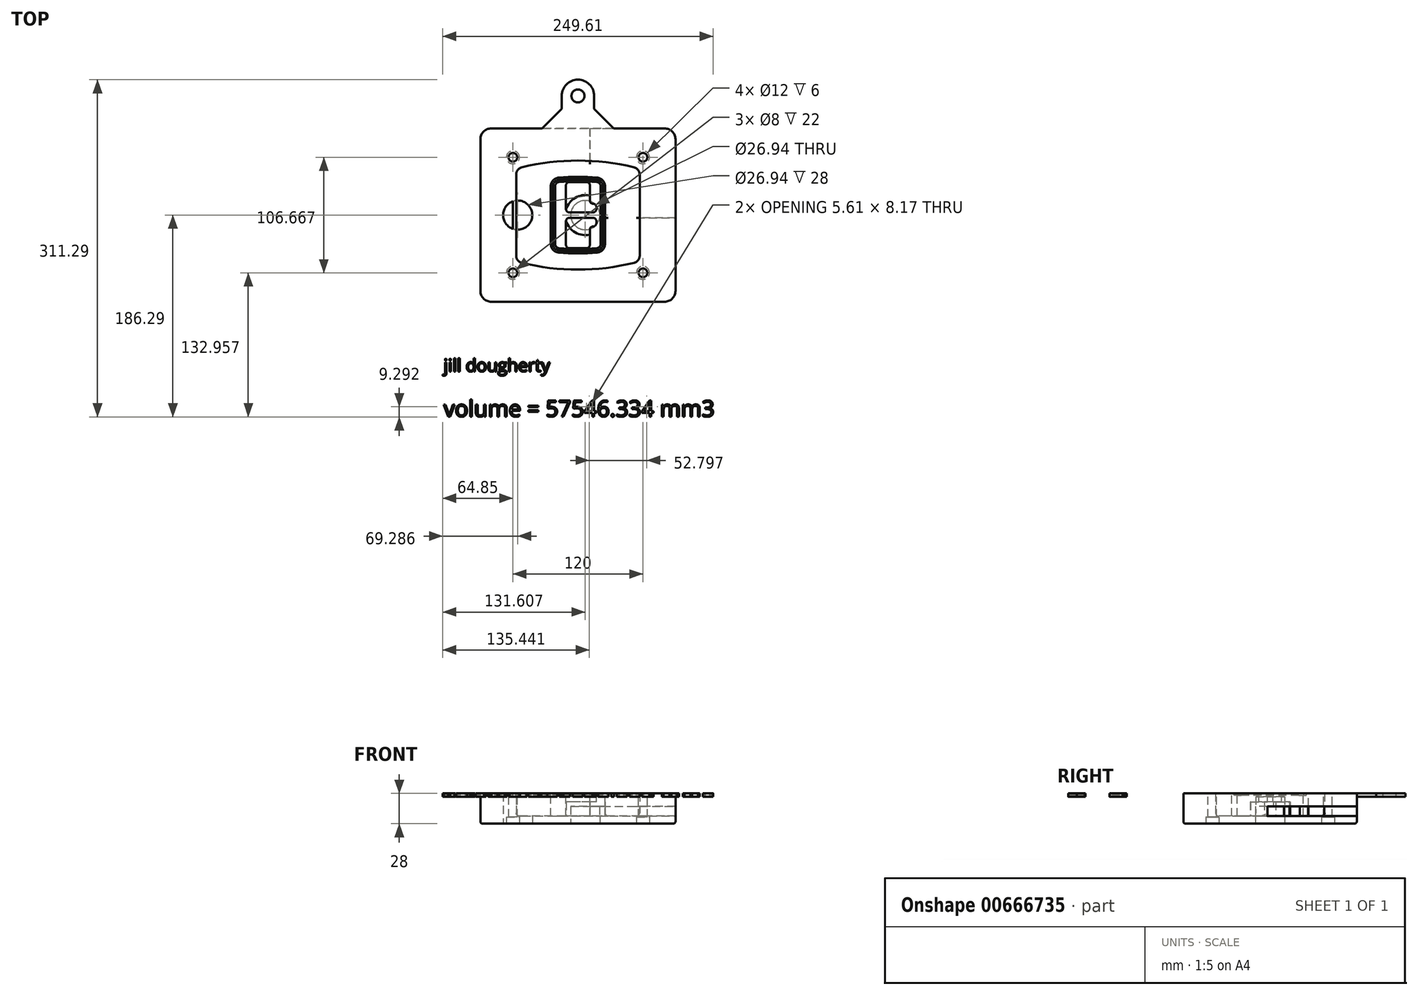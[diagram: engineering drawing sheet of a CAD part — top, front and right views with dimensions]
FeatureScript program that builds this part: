
annotation { "Feature Type Name" : "Feature", "Feature Type Description" : "" }
export const myFeature = defineFeature(function(context is Context, id is Id, definition is map)
    precondition{}
    {
        {
            var Q0;
            Q0=qCreatedBy(makeId("Top.planeOp"),FACE);
            var sketch = newSketch(context, id + "F0", { "sketchPlane" : qUnion([Q0])});
            skPoint(sketch, "E0.rect.middle", {"position": v(0, 0) * mm});
            skLineSegment(sketch, "E1.bottom", {"start": v(-80, -80) * mm, "end": v(80, -80) * mm});
            skLineSegment(sketch, "E1.top", {"start": v(-80, 80) * mm, "end": v(80, 80) * mm});
            skLineSegment(sketch, "E1.left", {"start": v(-90, -70) * mm, "end": v(-90, 70) * mm});
            skLineSegment(sketch, "E1.right", {"start": v(90, -70) * mm, "end": v(90, 70) * mm});
            skLineSegment(sketch, "E2", {"start": v(-90, 80) * mm, "end": v(90, -80) * mm, "construction": true});
            skLineSegment(sketch, "E3", {"start": v(90, 80) * mm, "end": v(-90, -80) * mm, "construction": true});
            skCircle(sketch, "E4", {"center": v(-60, 53.33) * mm, "radius": 4 * mm});
            skCircle(sketch, "E5", {"center": v(60, 53.33) * mm, "radius": 4 * mm});
            skCircle(sketch, "E6", {"center": v(60, -53.33) * mm, "radius": 4 * mm});
            skCircle(sketch, "E7", {"center": v(-60, -53.33) * mm, "radius": 4 * mm});
            skLineSegment(sketch, "E8", {"start": v(-60, 53.33) * mm, "end": v(60, 53.33) * mm, "construction": true});
            skLineSegment(sketch, "E9", {"start": v(60, 53.33) * mm, "end": v(60, -53.33) * mm, "construction": true});
            skLineSegment(sketch, "E10", {"start": v(60, -53.33) * mm, "end": v(-60, -53.33) * mm, "construction": true});
            skLineSegment(sketch, "E11", {"start": v(-60, -53.33) * mm, "end": v(-60, 53.33) * mm, "construction": true});
            skLineSegment(sketch, "E12", {"start": v(-60, 37.3) * mm, "end": v(-60, -37.3) * mm});
            skLineSegment(sketch, "E13", {"start": v(60, 37.3) * mm, "end": v(60, -37.3) * mm});
            skArc(sketch, "E14", {"start": v(52.38, 47.01) * mm, "mid": v(0, 53.33) * mm, "end": v(-52.38, 47.01) * mm});
            skArc(sketch, "E15", {"start": v(-52.38, -47.01) * mm, "mid": v(0, -53.33) * mm, "end": v(52.38, -47.01) * mm});
            skLineSegment(sketch, "E16", {"start": v(-60, 0) * mm, "end": v(60, 0) * mm, "construction": true});
            skPoint(sketch, "E17.visualSharp", {"position": v(-60, -45) * mm});
            skArc(sketch, "E17.filletArc", {"start": v(-60, -37.3) * mm, "mid": v(-57.87, -43.47) * mm, "end": v(-52.38, -47.01) * mm});
            skPoint(sketch, "E18.visualSharp", {"position": v(-60, 45) * mm});
            skArc(sketch, "E18.filletArc", {"start": v(-52.38, 47.01) * mm, "mid": v(-57.87, 43.47) * mm, "end": v(-60, 37.3) * mm});
            skPoint(sketch, "E19.visualSharp", {"position": v(60, 45) * mm});
            skArc(sketch, "E19.filletArc", {"start": v(60, 37.3) * mm, "mid": v(57.87, 43.47) * mm, "end": v(52.38, 47.01) * mm});
            skPoint(sketch, "E20.visualSharp", {"position": v(60, -45) * mm});
            skArc(sketch, "E20.filletArc", {"start": v(52.38, -47.01) * mm, "mid": v(57.87, -43.47) * mm, "end": v(60, -37.3) * mm});
            skPoint(sketch, "E21.visualSharp", {"position": v(-90, 80) * mm});
            skArc(sketch, "E21.filletArc", {"start": v(-80, 80) * mm, "mid": v(-87.07, 77.07) * mm, "end": v(-90, 70) * mm});
            skPoint(sketch, "E22.visualSharp", {"position": v(90, 80) * mm});
            skArc(sketch, "E22.filletArc", {"start": v(90, 70) * mm, "mid": v(87.07, 77.07) * mm, "end": v(80, 80) * mm});
            skPoint(sketch, "E23.visualSharp", {"position": v(90, -80) * mm});
            skArc(sketch, "E23.filletArc", {"start": v(80, -80) * mm, "mid": v(87.07, -77.07) * mm, "end": v(90, -70) * mm});
            skPoint(sketch, "E24.visualSharp", {"position": v(-90, -80) * mm});
            skArc(sketch, "E24.filletArc", {"start": v(-90, -70) * mm, "mid": v(-87.07, -77.07) * mm, "end": v(-80, -80) * mm});
            skArc(sketch, "E25.0", {"start": v(57, 37.3) * mm, "mid": v(55.5, 41.62) * mm, "end": v(51.67, 44.1) * mm});
            skLineSegment(sketch, "E25.1", {"start": v(57, 37.3) * mm, "end": v(57, -37.3) * mm});
            skArc(sketch, "E25.2", {"start": v(51.67, -44.1) * mm, "mid": v(55.5, -41.62) * mm, "end": v(57, -37.3) * mm});
            skArc(sketch, "E25.3", {"start": v(-51.67, -44.1) * mm, "mid": v(0, -50.33) * mm, "end": v(51.67, -44.1) * mm});
            skArc(sketch, "E25.4", {"start": v(-57, -37.3) * mm, "mid": v(-55.5, -41.62) * mm, "end": v(-51.67, -44.1) * mm});
            skArc(sketch, "E25.5", {"start": v(51.67, 44.1) * mm, "mid": v(0, 50.33) * mm, "end": v(-51.67, 44.1) * mm});
            skLineSegment(sketch, "E25.6", {"start": v(-57, 37.3) * mm, "end": v(-57, -37.3) * mm});
            skArc(sketch, "E25.7", {"start": v(-51.67, 44.1) * mm, "mid": v(-55.5, 41.62) * mm, "end": v(-57, 37.3) * mm});
            skArc(sketch, "E26.0", {"start": v(-53.33, 50.9) * mm, "mid": v(-61.01, 45.94) * mm, "end": v(-64, 37.3) * mm});
            skArc(sketch, "E26.1", {"start": v(53.33, 50.9) * mm, "mid": v(0, 57.33) * mm, "end": v(-53.33, 50.9) * mm});
            skArc(sketch, "E26.2", {"start": v(64, 37.3) * mm, "mid": v(61.01, 45.94) * mm, "end": v(53.33, 50.9) * mm});
            skLineSegment(sketch, "E26.3", {"start": v(64, 37.3) * mm, "end": v(64, -37.3) * mm});
            skArc(sketch, "E26.4", {"start": v(53.33, -50.9) * mm, "mid": v(61.01, -45.94) * mm, "end": v(64, -37.3) * mm});
            skLineSegment(sketch, "E26.5", {"start": v(-64, 37.3) * mm, "end": v(-64, -37.3) * mm});
            skArc(sketch, "E26.6", {"start": v(-53.33, -50.9) * mm, "mid": v(0, -57.33) * mm, "end": v(53.33, -50.9) * mm});
            skArc(sketch, "E26.7", {"start": v(-64, -37.3) * mm, "mid": v(-61.01, -45.94) * mm, "end": v(-53.33, -50.9) * mm});
            skSolve(sketch);
        }
        {
            var Q0;
            Q0=makeQuery(id+"F0.imprint","IMPRINT",FACE,{"disambiguationData":[TD([[makeQuery(id+"F0.imprint","IMPRINT",EDGE,{"derivedFrom":sQuery(id+"F0.wireOp",EDGE,"E1.bottom")}),1.0]])]});
            var Q1;
            Q1=makeQuery(id+"F0.imprint","IMPRINT",FACE,{"disambiguationData":[TD([[makeQuery(id+"F0.imprint","IMPRINT",EDGE,{"derivedFrom":sQuery(id+"F0.wireOp",EDGE,"E12")}),1.0]])]});
            var Q2;
            Q2=makeQuery(id+"F0.imprint","IMPRINT",FACE,{"disambiguationData":[TD([[makeQuery(id+"F0.imprint","IMPRINT",EDGE,{"derivedFrom":sQuery(id+"F0.wireOp",EDGE,"E25.0")}),1.0]])]});
            var Q3;
            Q3=makeQuery(id+"F0.imprint","IMPRINT",FACE,{"disambiguationData":[TD([[makeQuery(id+"F0.imprint","IMPRINT",EDGE,{"derivedFrom":sQuery(id+"F0.wireOp",EDGE,"E12")}),-1.0]])]});
            extrude(context, id + "F1", {"entities" : qUnion([Q0, Q1, Q2, Q3]), "oppositeDirection" : true, "depth" : 25 * mm});
        }
        {
            var Q0;
            Q0=makeQuery(id+"F0.imprint","IMPRINT",FACE,{"disambiguationData":[TD([[makeQuery(id+"F0.imprint","IMPRINT",EDGE,{"derivedFrom":sQuery(id+"F0.wireOp",EDGE,"E12")}),1.0]])]});
            extrude(context, id + "F2", {"entities" : qUnion([Q0]), "operationType" : NewBodyOperationType.ADD, "depth" : 3 * mm});
        }
        {
            var Q0;
            Q0=makeQuery(id+"F0.imprint","IMPRINT",FACE,{"disambiguationData":[TD([[makeQuery(id+"F0.imprint","IMPRINT",EDGE,{"derivedFrom":sQuery(id+"F0.wireOp",EDGE,"E25.0")}),1.0]])]});
            extrude(context, id + "F3", {"entities" : qUnion([Q0]), "operationType" : NewBodyOperationType.REMOVE, "oppositeDirection" : true, "depth" : 18 * mm});
        }
        {
            var Q0;
            Q0=makeQuery(id+"F2.opExtrude","CAP_FACE",FACE,{"disambiguationData":[OSD([sQuery(id+"F0.wireOp",EDGE,"E12"),sQuery(id+"F0.wireOp",EDGE,"E13"),sQuery(id+"F0.wireOp",EDGE,"E14"),sQuery(id+"F0.wireOp",EDGE,"E15"),sQuery(id+"F0.wireOp",EDGE,"E17.filletArc"),sQuery(id+"F0.wireOp",EDGE,"E18.filletArc"),sQuery(id+"F0.wireOp",EDGE,"E19.filletArc"),sQuery(id+"F0.wireOp",EDGE,"E20.filletArc"),sQuery(id+"F0.wireOp",EDGE,"E25.0"),sQuery(id+"F0.wireOp",EDGE,"E25.1"),sQuery(id+"F0.wireOp",EDGE,"E25.2"),sQuery(id+"F0.wireOp",EDGE,"E25.3"),sQuery(id+"F0.wireOp",EDGE,"E25.4"),sQuery(id+"F0.wireOp",EDGE,"E25.5"),sQuery(id+"F0.wireOp",EDGE,"E25.6"),sQuery(id+"F0.wireOp",EDGE,"E25.7")])],"isStart":false});
            var sketch = newSketch(context, id + "F4", { "sketchPlane" : qUnion([Q0])});
            skArc(sketch, "E27.0", {"start": v(-17.7, -34.56) * mm, "mid": v(0, -35.33) * mm, "end": v(17.7, -34.56) * mm});
            skArc(sketch, "E28.0", {"start": v(17.7, 34.56) * mm, "mid": v(0, 35.33) * mm, "end": v(-17.7, 34.56) * mm});
            skLineSegment(sketch, "E29", {"start": v(-25, 26.59) * mm, "end": v(-25, -26.59) * mm});
            skLineSegment(sketch, "E30", {"start": v(25, 26.59) * mm, "end": v(25, -26.59) * mm});
            skLineSegment(sketch, "E31", {"start": v(-25, 33.78) * mm, "end": v(25, 33.78) * mm, "construction": true});
            skLineSegment(sketch, "E32", {"start": v(-25, -33.78) * mm, "end": v(25, -33.78) * mm, "construction": true});
            skPoint(sketch, "E33.visualSharp", {"position": v(-25, 33.78) * mm});
            skArc(sketch, "E33.filletArc", {"start": v(-17.7, 34.56) * mm, "mid": v(-22.9, 32) * mm, "end": v(-25, 26.59) * mm});
            skPoint(sketch, "E34.visualSharp", {"position": v(25, 33.78) * mm});
            skArc(sketch, "E34.filletArc", {"start": v(25, 26.59) * mm, "mid": v(22.9, 32) * mm, "end": v(17.7, 34.56) * mm});
            skPoint(sketch, "E35.visualSharp", {"position": v(25, -33.78) * mm});
            skArc(sketch, "E35.filletArc", {"start": v(17.7, -34.56) * mm, "mid": v(22.9, -32) * mm, "end": v(25, -26.59) * mm});
            skPoint(sketch, "E36.visualSharp", {"position": v(-25, -33.78) * mm});
            skArc(sketch, "E36.filletArc", {"start": v(-25, -26.59) * mm, "mid": v(-22.9, -32) * mm, "end": v(-17.7, -34.56) * mm});
            skArc(sketch, "E37.0", {"start": v(51.67, 44.1) * mm, "mid": v(0, 50.33) * mm, "end": v(-51.67, 44.1) * mm});
            skArc(sketch, "E37.1", {"start": v(-51.67, 44.1) * mm, "mid": v(-55.5, 41.62) * mm, "end": v(-57, 37.3) * mm});
            skLineSegment(sketch, "E37.2", {"start": v(-57, 37.3) * mm, "end": v(-57, -37.3) * mm});
            skArc(sketch, "E37.3", {"start": v(-57, -37.3) * mm, "mid": v(-55.5, -41.62) * mm, "end": v(-51.67, -44.1) * mm});
            skArc(sketch, "E37.4", {"start": v(-51.67, -44.1) * mm, "mid": v(0, -50.33) * mm, "end": v(51.67, -44.1) * mm});
            skArc(sketch, "E37.5", {"start": v(51.67, -44.1) * mm, "mid": v(55.5, -41.62) * mm, "end": v(57, -37.3) * mm});
            skLineSegment(sketch, "E37.6", {"start": v(57, 37.3) * mm, "end": v(57, -37.3) * mm});
            skArc(sketch, "E37.7", {"start": v(57, 37.3) * mm, "mid": v(55.5, 41.62) * mm, "end": v(51.67, 44.1) * mm});
            skLineSegment(sketch, "E38.0", {"start": v(23, 26.59) * mm, "end": v(23, -26.59) * mm});
            skArc(sketch, "E38.1", {"start": v(17.53, -32.56) * mm, "mid": v(21.42, -30.64) * mm, "end": v(23, -26.59) * mm});
            skArc(sketch, "E38.2", {"start": v(-17.53, -32.56) * mm, "mid": v(0, -33.33) * mm, "end": v(17.53, -32.56) * mm});
            skArc(sketch, "E38.3", {"start": v(-23, -26.59) * mm, "mid": v(-21.42, -30.64) * mm, "end": v(-17.53, -32.56) * mm});
            skLineSegment(sketch, "E38.4", {"start": v(-23, 26.59) * mm, "end": v(-23, -26.59) * mm});
            skArc(sketch, "E38.5", {"start": v(23, 26.59) * mm, "mid": v(21.42, 30.64) * mm, "end": v(17.53, 32.56) * mm});
            skArc(sketch, "E38.6", {"start": v(-17.53, 32.56) * mm, "mid": v(-21.42, 30.64) * mm, "end": v(-23, 26.59) * mm});
            skArc(sketch, "E38.7", {"start": v(17.53, 32.56) * mm, "mid": v(0, 33.33) * mm, "end": v(-17.53, 32.56) * mm});
            skArc(sketch, "E39.0", {"start": v(21, 26.59) * mm, "mid": v(19.95, 29.29) * mm, "end": v(17.35, 30.57) * mm});
            skLineSegment(sketch, "E39.1", {"start": v(21, 26.59) * mm, "end": v(21, -26.59) * mm});
            skArc(sketch, "E39.2", {"start": v(17.35, -30.57) * mm, "mid": v(19.95, -29.29) * mm, "end": v(21, -26.59) * mm});
            skArc(sketch, "E39.3", {"start": v(-17.35, -30.57) * mm, "mid": v(0, -31.33) * mm, "end": v(17.35, -30.57) * mm});
            skArc(sketch, "E39.4", {"start": v(-21, -26.59) * mm, "mid": v(-19.95, -29.29) * mm, "end": v(-17.35, -30.57) * mm});
            skArc(sketch, "E39.5", {"start": v(17.35, 30.57) * mm, "mid": v(0, 31.33) * mm, "end": v(-17.35, 30.57) * mm});
            skLineSegment(sketch, "E39.6", {"start": v(-21, 26.59) * mm, "end": v(-21, -26.59) * mm});
            skArc(sketch, "E39.7", {"start": v(-17.35, 30.57) * mm, "mid": v(-19.95, 29.29) * mm, "end": v(-21, 26.59) * mm});
            skLineSegment(sketch, "E40", {"start": v(-25, 0) * mm, "end": v(25, 0) * mm, "construction": true});
            skLineSegment(sketch, "E41", {"start": v(-11, 5.5) * mm, "end": v(-11, 27.5) * mm});
            skLineSegment(sketch, "E42", {"start": v(-8, 30.5) * mm, "end": v(8, 30.5) * mm});
            skLineSegment(sketch, "E43", {"start": v(11, 27.5) * mm, "end": v(11, 13.5) * mm});
            skLineSegment(sketch, "E44", {"start": v(14, 10.5) * mm, "end": v(14, 10.5) * mm});
            skLineSegment(sketch, "E45", {"start": v(17, 7.5) * mm, "end": v(17, 5.5) * mm});
            skLineSegment(sketch, "E46", {"start": v(14, 2.5) * mm, "end": v(-8, 2.5) * mm});
            skPoint(sketch, "E47.visualSharp", {"position": v(-11, 30.5) * mm});
            skArc(sketch, "E47.filletArc", {"start": v(-8, 30.5) * mm, "mid": v(-10.12, 29.62) * mm, "end": v(-11, 27.5) * mm});
            skPoint(sketch, "E48.visualSharp", {"position": v(11, 30.5) * mm});
            skArc(sketch, "E48.filletArc", {"start": v(11, 27.5) * mm, "mid": v(10.12, 29.62) * mm, "end": v(8, 30.5) * mm});
            skPoint(sketch, "E49.visualSharp", {"position": v(11, 10.5) * mm});
            skArc(sketch, "E49.filletArc", {"start": v(11, 13.5) * mm, "mid": v(11.88, 11.38) * mm, "end": v(14, 10.5) * mm});
            skPoint(sketch, "E50.visualSharp", {"position": v(17, 10.5) * mm});
            skArc(sketch, "E50.filletArc", {"start": v(17, 7.5) * mm, "mid": v(16.12, 9.62) * mm, "end": v(14, 10.5) * mm});
            skPoint(sketch, "E51.visualSharp", {"position": v(17, 2.5) * mm});
            skArc(sketch, "E51.filletArc", {"start": v(14, 2.5) * mm, "mid": v(16.12, 3.38) * mm, "end": v(17, 5.5) * mm});
            skPoint(sketch, "E52.visualSharp", {"position": v(-11, 2.5) * mm});
            skArc(sketch, "E52.filletArc", {"start": v(-11, 5.5) * mm, "mid": v(-10.12, 3.38) * mm, "end": v(-8, 2.5) * mm});
            skLineSegment(sketch, "E53.0.MirrorCS", {"start": v(14, -2.5) * mm, "end": v(-8, -2.5) * mm});
            skArc(sketch, "E54.0.MirrorCS", {"start": v(-11, -5.5) * mm, "mid": v(-10.12, -3.38) * mm, "end": v(-8, -2.5) * mm});
            skLineSegment(sketch, "E55.0.MirrorCS", {"start": v(-11, -5.5) * mm, "end": v(-11, -27.5) * mm});
            skArc(sketch, "E56.0.MirrorCS", {"start": v(-8, -30.5) * mm, "mid": v(-10.12, -29.62) * mm, "end": v(-11, -27.5) * mm});
            skLineSegment(sketch, "E57.0.MirrorCS", {"start": v(-8, -30.5) * mm, "end": v(8, -30.5) * mm});
            skArc(sketch, "E58.0.MirrorCS", {"start": v(11, -27.5) * mm, "mid": v(10.12, -29.62) * mm, "end": v(8, -30.5) * mm});
            skLineSegment(sketch, "E59.0.MirrorCS", {"start": v(11, -27.5) * mm, "end": v(11, -13.5) * mm});
            skArc(sketch, "E60.0.MirrorCS", {"start": v(11, -13.5) * mm, "mid": v(11.88, -11.38) * mm, "end": v(14, -10.5) * mm});
            skArc(sketch, "E61.0.MirrorCS", {"start": v(17, -7.5) * mm, "mid": v(16.12, -9.62) * mm, "end": v(14, -10.5) * mm});
            skLineSegment(sketch, "E62.0.MirrorCS", {"start": v(17, -7.5) * mm, "end": v(17, -5.5) * mm});
            skArc(sketch, "E63.0.MirrorCS", {"start": v(14, -2.5) * mm, "mid": v(16.12, -3.38) * mm, "end": v(17, -5.5) * mm});
            skSolve(sketch);
        }
        {
            var Q0;
            Q0=makeQuery(id+"F4.imprint","IMPRINT",FACE,{"disambiguationData":[TD([[makeQuery(id+"F4.imprint","IMPRINT",EDGE,{"derivedFrom":sQuery(id+"F4.wireOp",EDGE,"E27.0")}),1.0]])]});
            var Q1;
            Q1=makeQuery(id+"F4.imprint","IMPRINT",FACE,{"disambiguationData":[TD([[makeQuery(id+"F4.imprint","IMPRINT",EDGE,{"derivedFrom":sQuery(id+"F4.wireOp",EDGE,"E38.0")}),-1.0]])]});
            var Q2;
            Q2=makeQuery(id+"F4.imprint","IMPRINT",FACE,{"disambiguationData":[TD([[makeQuery(id+"F4.imprint","IMPRINT",EDGE,{"derivedFrom":sQuery(id+"F4.wireOp",EDGE,"E39.0")}),1.0]])]});
            extrude(context, id + "F5", {"entities" : qUnion([Q0, Q1, Q2]), "operationType" : NewBodyOperationType.ADD, "endBound" : BoundingType.UP_TO_NEXT, "oppositeDirection" : true, "depth" : 25 * mm});
        }
        {
            var Q0;
            Q0=makeQuery(id+"F4.imprint","IMPRINT",FACE,{"disambiguationData":[TD([[makeQuery(id+"F4.imprint","IMPRINT",EDGE,{"derivedFrom":sQuery(id+"F4.wireOp",EDGE,"E38.0")}),-1.0]])]});
            extrude(context, id + "F6", {"entities" : qUnion([Q0]), "operationType" : NewBodyOperationType.REMOVE, "oppositeDirection" : true, "depth" : 2 * mm});
        }
        {
            var Q0;
            Q0=makeQuery(id+"F1.opExtrude","CAP_FACE",FACE,{"disambiguationData":[OSD([sQuery(id+"F0.wireOp",EDGE,"E1.bottom"),sQuery(id+"F0.wireOp",EDGE,"E1.top"),sQuery(id+"F0.wireOp",EDGE,"E1.left"),sQuery(id+"F0.wireOp",EDGE,"E1.right"),sQuery(id+"F0.wireOp",EDGE,"E4"),sQuery(id+"F0.wireOp",EDGE,"E5"),sQuery(id+"F0.wireOp",EDGE,"E6"),sQuery(id+"F0.wireOp",EDGE,"E7"),sQuery(id+"F0.wireOp",EDGE,"E21.filletArc"),sQuery(id+"F0.wireOp",EDGE,"E22.filletArc"),sQuery(id+"F0.wireOp",EDGE,"E23.filletArc"),sQuery(id+"F0.wireOp",EDGE,"E24.filletArc")])],"isStart":false});
            var sketch = newSketch(context, id + "F7", { "sketchPlane" : qUnion([Q0])});
            skCircle(sketch, "E64", {"center": v(6.76, 0) * mm, "radius": 13.47 * mm});
            skCircle(sketch, "E65", {"center": v(-55.56, 0) * mm, "radius": 13.47 * mm});
            skLineSegment(sketch, "E66", {"start": v(90, 0) * mm, "end": v(-90, 0) * mm});
            skCircle(sketch, "E67", {"center": v(6.76, 0) * mm, "radius": 18.47 * mm});
            skCircle(sketch, "E68", {"center": v(60, -53.33) * mm, "radius": 6 * mm});
            skCircle(sketch, "E69", {"center": v(-60, -53.33) * mm, "radius": 6 * mm});
            skCircle(sketch, "E70", {"center": v(-60, 53.33) * mm, "radius": 6 * mm});
            skCircle(sketch, "E71", {"center": v(60, 53.33) * mm, "radius": 6 * mm});
            skSolve(sketch);
        }
        {
            var Q0;
            {var subQ1=sQuery(id+"F7.wireOp",EDGE,"E66");var subQ4=sQuery(id+"F7.wireOp",EDGE,"E64");var subQ6=makeQuery(id+"F7.imprint","INTERSECT",VERTEX,{"disambiguationData":[OD(0.0)],"derivedFrom":[subQ4,subQ1]});Q0=makeQuery(id+"F7.imprint","IMPRINT",FACE,{"disambiguationData":[TD([[makeQuery(id+"F7.imprint","IMPRINT",EDGE,{"disambiguationData":[TD([[subQ6,-1.0]])],"derivedFrom":subQ4}),-1.0]])]});}
            var Q1;
            {var subQ0=sQuery(id+"F7.wireOp",EDGE,"E66");var subQ1=sQuery(id+"F7.wireOp",EDGE,"E64");var subQ3=makeQuery(id+"F7.imprint","INTERSECT",VERTEX,{"disambiguationData":[OD(0.0)],"derivedFrom":[subQ1,subQ0]});Q1=makeQuery(id+"F7.imprint","IMPRINT",FACE,{"disambiguationData":[TD([[makeQuery(id+"F7.imprint","IMPRINT",EDGE,{"disambiguationData":[TD([[subQ3,-1.0]])],"derivedFrom":subQ1}),1.0]])]});}
            var Q2;
            {var subQ0=sQuery(id+"F7.wireOp",EDGE,"E66");var subQ1=sQuery(id+"F7.wireOp",EDGE,"E64");var subQ3=makeQuery(id+"F7.imprint","INTERSECT",VERTEX,{"disambiguationData":[OD(0.0)],"derivedFrom":[subQ1,subQ0]});Q2=makeQuery(id+"F7.imprint","IMPRINT",FACE,{"disambiguationData":[TD([[makeQuery(id+"F7.imprint","IMPRINT",EDGE,{"disambiguationData":[TD([[subQ3,1.0]])],"derivedFrom":subQ1}),1.0]])]});}
            var Q3;
            {var subQ1=sQuery(id+"F7.wireOp",EDGE,"E66");var subQ4=sQuery(id+"F7.wireOp",EDGE,"E64");var subQ6=makeQuery(id+"F7.imprint","INTERSECT",VERTEX,{"disambiguationData":[OD(0.0)],"derivedFrom":[subQ4,subQ1]});Q3=makeQuery(id+"F7.imprint","IMPRINT",FACE,{"disambiguationData":[TD([[makeQuery(id+"F7.imprint","IMPRINT",EDGE,{"disambiguationData":[TD([[subQ6,1.0]])],"derivedFrom":subQ4}),-1.0]])]});}
            extrude(context, id + "F8", {"entities" : qUnion([Q0, Q1, Q2, Q3]), "operationType" : NewBodyOperationType.ADD, "oppositeDirection" : true, "depth" : 20 * mm});
        }
        {
            var Q0;
            {var subQ0=sQuery(id+"F7.wireOp",EDGE,"E66");var subQ1=sQuery(id+"F7.wireOp",EDGE,"E64");var subQ3=makeQuery(id+"F7.imprint","INTERSECT",VERTEX,{"disambiguationData":[OD(0.0)],"derivedFrom":[subQ1,subQ0]});Q0=makeQuery(id+"F7.imprint","IMPRINT",FACE,{"disambiguationData":[TD([[makeQuery(id+"F7.imprint","IMPRINT",EDGE,{"disambiguationData":[TD([[subQ3,-1.0]])],"derivedFrom":subQ1}),1.0]])]});}
            var Q1;
            {var subQ0=sQuery(id+"F7.wireOp",EDGE,"E66");var subQ1=sQuery(id+"F7.wireOp",EDGE,"E64");var subQ3=makeQuery(id+"F7.imprint","INTERSECT",VERTEX,{"disambiguationData":[OD(0.0)],"derivedFrom":[subQ1,subQ0]});Q1=makeQuery(id+"F7.imprint","IMPRINT",FACE,{"disambiguationData":[TD([[makeQuery(id+"F7.imprint","IMPRINT",EDGE,{"disambiguationData":[TD([[subQ3,1.0]])],"derivedFrom":subQ1}),1.0]])]});}
            extrude(context, id + "F9", {"entities" : qUnion([Q0, Q1]), "operationType" : NewBodyOperationType.REMOVE, "oppositeDirection" : true, "depth" : 16 * mm});
        }
        {
            var Q0;
            {var subQ0=sQuery(id+"F7.wireOp",EDGE,"E66");var subQ1=sQuery(id+"F7.wireOp",EDGE,"E65");var subQ3=makeQuery(id+"F7.imprint","INTERSECT",VERTEX,{"disambiguationData":[OD(0.0)],"derivedFrom":[subQ1,subQ0]});Q0=makeQuery(id+"F7.imprint","IMPRINT",FACE,{"disambiguationData":[TD([[makeQuery(id+"F7.imprint","IMPRINT",EDGE,{"disambiguationData":[TD([[subQ3,-1.0]])],"derivedFrom":subQ1}),1.0]])]});}
            var Q1;
            {var subQ0=sQuery(id+"F7.wireOp",EDGE,"E66");var subQ1=sQuery(id+"F7.wireOp",EDGE,"E65");var subQ3=makeQuery(id+"F7.imprint","INTERSECT",VERTEX,{"disambiguationData":[OD(0.0)],"derivedFrom":[subQ1,subQ0]});Q1=makeQuery(id+"F7.imprint","IMPRINT",FACE,{"disambiguationData":[TD([[makeQuery(id+"F7.imprint","IMPRINT",EDGE,{"disambiguationData":[TD([[subQ3,1.0]])],"derivedFrom":subQ1}),1.0]])]});}
            extrude(context, id + "F10", {"entities" : qUnion([Q0, Q1]), "operationType" : NewBodyOperationType.REMOVE, "oppositeDirection" : true, "depth" : 25 * mm});
        }
        {
            var Q0;
            Q0=makeQuery(id+"F7.imprint","IMPRINT",FACE,{"disambiguationData":[TD([[makeQuery(id+"F7.imprint","IMPRINT",EDGE,{"derivedFrom":sQuery(id+"F7.wireOp",EDGE,"E68")}),1.0]])]});
            var Q1;
            Q1=makeQuery(id+"F7.imprint","IMPRINT",FACE,{"disambiguationData":[TD([[makeQuery(id+"F7.imprint","IMPRINT",EDGE,{"derivedFrom":makeQuery(id+"F1.opExtrude","CAP_EDGE",EDGE,{"disambiguationData":[OSD([sQuery(id+"F0.wireOp",EDGE,"E5")])],"isStart":false})}),-1.0]])]});
            var Q2;
            Q2=makeQuery(id+"F7.imprint","IMPRINT",FACE,{"disambiguationData":[TD([[makeQuery(id+"F7.imprint","IMPRINT",EDGE,{"derivedFrom":sQuery(id+"F7.wireOp",EDGE,"E69")}),1.0]])]});
            var Q3;
            Q3=makeQuery(id+"F7.imprint","IMPRINT",FACE,{"disambiguationData":[TD([[makeQuery(id+"F7.imprint","IMPRINT",EDGE,{"derivedFrom":makeQuery(id+"F1.opExtrude","CAP_EDGE",EDGE,{"disambiguationData":[OSD([sQuery(id+"F0.wireOp",EDGE,"E4")])],"isStart":false})}),-1.0]])]});
            var Q4;
            Q4=makeQuery(id+"F7.imprint","IMPRINT",FACE,{"disambiguationData":[TD([[makeQuery(id+"F7.imprint","IMPRINT",EDGE,{"derivedFrom":sQuery(id+"F7.wireOp",EDGE,"E70")}),1.0]])]});
            var Q5;
            Q5=makeQuery(id+"F7.imprint","IMPRINT",FACE,{"disambiguationData":[TD([[makeQuery(id+"F7.imprint","IMPRINT",EDGE,{"derivedFrom":makeQuery(id+"F1.opExtrude","CAP_EDGE",EDGE,{"disambiguationData":[OSD([sQuery(id+"F0.wireOp",EDGE,"E7")])],"isStart":false})}),-1.0]])]});
            var Q6;
            Q6=makeQuery(id+"F7.imprint","IMPRINT",FACE,{"disambiguationData":[TD([[makeQuery(id+"F7.imprint","IMPRINT",EDGE,{"derivedFrom":sQuery(id+"F7.wireOp",EDGE,"E71")}),1.0]])]});
            var Q7;
            Q7=makeQuery(id+"F7.imprint","IMPRINT",FACE,{"disambiguationData":[TD([[makeQuery(id+"F7.imprint","IMPRINT",EDGE,{"derivedFrom":makeQuery(id+"F1.opExtrude","CAP_EDGE",EDGE,{"disambiguationData":[OSD([sQuery(id+"F0.wireOp",EDGE,"E6")])],"isStart":false})}),-1.0]])]});
            extrude(context, id + "F11", {"entities" : qUnion([Q0, Q1, Q2, Q3, Q4, Q5, Q6, Q7]), "operationType" : NewBodyOperationType.REMOVE, "oppositeDirection" : true, "depth" : 6 * mm});
        }
        {
            var Q0;
            Q0=makeQuery(id+"F9.boolean.opBoolean","COPY",FACE,{"derivedFrom":makeQuery(id+"F9.opExtrude","CAP_FACE",FACE,{"disambiguationData":[OSD([sQuery(id+"F7.wireOp",EDGE,"E64")])],"isStart":false})});
            var sketch = newSketch(context, id + "F12", { "sketchPlane" : qUnion([Q0])});
            skArc(sketch, "E72.0", {"start": v(11, -88.19) * mm, "mid": v(97.1, -83.6) * mm, "end": v(92.5, 2.5) * mm});
            skLineSegment(sketch, "E72.1", {"start": v(11, -17.97) * mm, "end": v(11, -17.97) * mm});
            skLineSegment(sketch, "E73", {"start": v(92.5, -105.13) * mm, "end": v(102.3, -105.13) * mm});
            skLineSegment(sketch, "E74.0", {"start": v(92.5, 2.5) * mm, "end": v(14, 2.5) * mm});
            skArc(sketch, "E74.1", {"start": v(14, 2.5) * mm, "mid": v(16.12, 3.38) * mm, "end": v(17, 5.5) * mm});
            skLineSegment(sketch, "E74.2", {"start": v(17, 7.5) * mm, "end": v(17, 5.5) * mm});
            skArc(sketch, "E74.3", {"start": v(17, 7.5) * mm, "mid": v(16.12, 9.62) * mm, "end": v(14, 10.5) * mm});
            skArc(sketch, "E74.4", {"start": v(11, 13.5) * mm, "mid": v(11.88, 11.38) * mm, "end": v(14, 10.5) * mm});
            skLineSegment(sketch, "E74.5", {"start": v(11, 13.5) * mm, "end": v(11, -88.19) * mm});
            skLineSegment(sketch, "E74.7", {"start": v(92.5, -2.5) * mm, "end": v(14, -2.5) * mm});
            skArc(sketch, "E74.8", {"start": v(14, -2.5) * mm, "mid": v(16.12, -3.38) * mm, "end": v(17, -5.5) * mm});
            skLineSegment(sketch, "E74.9", {"start": v(17, -7.5) * mm, "end": v(17, -5.5) * mm});
            skArc(sketch, "E74.10", {"start": v(17, -7.5) * mm, "mid": v(16.12, -9.62) * mm, "end": v(14, -10.5) * mm});
            skArc(sketch, "E74.11", {"start": v(11, -13.5) * mm, "mid": v(11.88, -11.38) * mm, "end": v(14, -10.5) * mm});
            skLineSegment(sketch, "E74.12", {"start": v(11, -17.97) * mm, "end": v(11, -13.5) * mm});
            skPoint(sketch, "E75.orphan", {"position": v(11, -27.5) * mm});
            skPoint(sketch, "E76.orphan", {"position": v(-8, -2.5) * mm});
            skPoint(sketch, "E77.orphan", {"position": v(-8, 2.5) * mm});
            skPoint(sketch, "E78.orphan", {"position": v(11, 27.5) * mm});
            skSolve(sketch);
        }
        {
            var Q0;
            {var subQ7=sQuery(id+"F12.wireOp",EDGE,"E72.0");var subQ14=sQuery(id+"F12.wireOp",EDGE,"E72.1");var subQ16=sQuery(id+"F12.wireOp",EDGE,"E74.1");var subQ18=sQuery(id+"F12.wireOp",EDGE,"E74.8");Q0=qUnion([makeQuery(id+"F12.imprint","IMPRINT",FACE,{"disambiguationData":[TD([[makeQuery(id+"F12.imprint","IMPRINT",EDGE,{"derivedFrom":subQ7}),1.0]])]}),makeQuery(id+"F12.imprint","IMPRINT",FACE,{"disambiguationData":[TD([[makeQuery(id+"F12.imprint","IMPRINT",EDGE,{"derivedFrom":subQ14}),1.0]])]}),makeQuery(id+"F12.imprint","IMPRINT",FACE,{"disambiguationData":[TD([[makeQuery(id+"F12.imprint","IMPRINT",EDGE,{"derivedFrom":subQ16}),1.0]])]}),makeQuery(id+"F12.imprint","IMPRINT",FACE,{"disambiguationData":[TD([[makeQuery(id+"F12.imprint","IMPRINT",EDGE,{"derivedFrom":subQ18}),-1.0]])]})]);}
            var Q1;
            Q1=makeQuery(id+"F5.boolean.opBoolean","SPLIT",FACE,{"disambiguationData":[TD([makeQuery(id+"F5.opExtrude","SWEPT_FACE",FACE,{"disambiguationData":[OSD([sQuery(id+"F4.wireOp",EDGE,"E41")])]})])],"derivedFrom":makeQuery(id+"F3.boolean.opBoolean","COPY",FACE,{"derivedFrom":makeQuery(id+"F3.opExtrude","CAP_FACE",FACE,{"disambiguationData":[OSD([sQuery(id+"F0.wireOp",EDGE,"E25.0"),sQuery(id+"F0.wireOp",EDGE,"E25.1"),sQuery(id+"F0.wireOp",EDGE,"E25.2"),sQuery(id+"F0.wireOp",EDGE,"E25.3"),sQuery(id+"F0.wireOp",EDGE,"E25.4"),sQuery(id+"F0.wireOp",EDGE,"E25.5"),sQuery(id+"F0.wireOp",EDGE,"E25.6"),sQuery(id+"F0.wireOp",EDGE,"E25.7")])],"isStart":false})})});
            extrude(context, id + "F13", {"entities" : qUnion([Q0]), "operationType" : NewBodyOperationType.REMOVE, "endBound" : BoundingType.UP_TO_SURFACE, "endBoundEntityFace" : qUnion([Q1]), "depth" : 25 * mm});
        }
        {
            var Q0;
            Q0=makeQuery(id+"F3.boolean.opBoolean","COPY",EDGE,{"derivedFrom":makeQuery(id+"F3.opExtrude","CAP_EDGE",EDGE,{"disambiguationData":[OSD([sQuery(id+"F0.wireOp",EDGE,"E25.6")])],"isStart":false})});
            var Q1;
            Q1=makeQuery(id+"F8.boolean.opBoolean","INTERSECT",EDGE,{"derivedFrom":[makeQuery(id+"F5.opExtrude","SWEPT_FACE",FACE,{"disambiguationData":[OSD([sQuery(id+"F4.wireOp",EDGE,"E30")])]}),makeQuery(id+"F8.opExtrude","CAP_FACE",FACE,{"disambiguationData":[OSD([sQuery(id+"F7.wireOp",EDGE,"E67")])],"isStart":false})]});
            var Q2;
            Q2=makeQuery(id+"F8.boolean.opBoolean","INTERSECT",EDGE,{"disambiguationData":[OD(1.0)],"derivedFrom":[makeQuery(id+"F5.opExtrude","SWEPT_FACE",FACE,{"disambiguationData":[OSD([sQuery(id+"F4.wireOp",EDGE,"E30")])]}),makeQuery(id+"F8.opExtrude","SWEPT_FACE",FACE,{"disambiguationData":[OSD([sQuery(id+"F7.wireOp",EDGE,"E67")])]})]});
            var Q3;
            {var subQ0=makeQuery(id+"F3.boolean.opBoolean","COPY",FACE,{"derivedFrom":makeQuery(id+"F3.opExtrude","CAP_FACE",FACE,{"disambiguationData":[OSD([sQuery(id+"F0.wireOp",EDGE,"E25.0"),sQuery(id+"F0.wireOp",EDGE,"E25.1"),sQuery(id+"F0.wireOp",EDGE,"E25.2"),sQuery(id+"F0.wireOp",EDGE,"E25.3"),sQuery(id+"F0.wireOp",EDGE,"E25.4"),sQuery(id+"F0.wireOp",EDGE,"E25.5"),sQuery(id+"F0.wireOp",EDGE,"E25.6"),sQuery(id+"F0.wireOp",EDGE,"E25.7")])],"isStart":false})});var subQ1=sQuery(id+"F4.wireOp",EDGE,"E30");Q3=makeQuery(id+"F8.boolean.opBoolean","SPLIT",EDGE,{"disambiguationData":[TD([makeQuery(id+"F5.opExtrude","SWEPT_FACE",FACE,{"disambiguationData":[OSD([sQuery(id+"F4.wireOp",EDGE,"E35.filletArc")])]})])],"derivedFrom":makeQuery(id+"F5.opExtrude","TWEAK_EDGE",EDGE,{"derivedFrom":[subQ0,makeQuery(id+"F4.imprint","IMPRINT",EDGE,{"derivedFrom":subQ1})]})});}
            var Q4;
            {var subQ0=sQuery(id+"F0.wireOp",EDGE,"E25.0");var subQ1=sQuery(id+"F0.wireOp",EDGE,"E25.1");var subQ2=sQuery(id+"F0.wireOp",EDGE,"E25.2");var subQ3=sQuery(id+"F0.wireOp",EDGE,"E25.3");var subQ4=sQuery(id+"F0.wireOp",EDGE,"E25.4");var subQ5=sQuery(id+"F0.wireOp",EDGE,"E25.5");var subQ6=sQuery(id+"F0.wireOp",EDGE,"E25.6");var subQ7=sQuery(id+"F0.wireOp",EDGE,"E25.7");Q4=makeQuery(id+"F8.boolean.opBoolean","INTERSECT",EDGE,{"derivedFrom":[makeQuery(id+"F5.boolean.opBoolean","SPLIT",FACE,{"disambiguationData":[TD([makeQuery(id+"F2.opExtrude","SWEPT_FACE",FACE,{"disambiguationData":[OSD([subQ0])]})])],"derivedFrom":makeQuery(id+"F3.boolean.opBoolean","COPY",FACE,{"derivedFrom":makeQuery(id+"F3.opExtrude","CAP_FACE",FACE,{"disambiguationData":[OSD([subQ0,subQ1,subQ2,subQ3,subQ4,subQ5,subQ6,subQ7])],"isStart":false})})}),makeQuery(id+"F8.opExtrude","SWEPT_FACE",FACE,{"disambiguationData":[OSD([sQuery(id+"F7.wireOp",EDGE,"E67")])]})]});}
            var Q5;
            Q5=makeQuery(id+"F8.boolean.opBoolean","INTERSECT",EDGE,{"disambiguationData":[OD(0.0)],"derivedFrom":[makeQuery(id+"F5.opExtrude","SWEPT_FACE",FACE,{"disambiguationData":[OSD([sQuery(id+"F4.wireOp",EDGE,"E30")])]}),makeQuery(id+"F8.opExtrude","SWEPT_FACE",FACE,{"disambiguationData":[OSD([sQuery(id+"F7.wireOp",EDGE,"E67")])]})]});
            fillet(context, id + "F14", {"entities" : qUnion([Q0, Q1, Q2, Q3, Q4, Q5]), "radius" : 3 * mm, "tangentPropagation" : true, "allowEdgeOverflow" : false});
        }
        {
            var Q0;
            Q0=makeQuery(id+"F1.opExtrude","CAP_EDGE",EDGE,{"disambiguationData":[OSD([sQuery(id+"F0.wireOp",EDGE,"E1.bottom")])],"isStart":false});
            fillet(context, id + "F15", {"entities" : qUnion([Q0]), "radius" : 2 * mm, "tangentPropagation" : true, "allowEdgeOverflow" : false});
        }
        {
            var Q0;
            {var subQ0=sQuery(id+"F0.wireOp",EDGE,"E21.filletArc");var subQ1=sQuery(id+"F0.wireOp",EDGE,"E7");var subQ2=sQuery(id+"F0.wireOp",EDGE,"E6");var subQ3=sQuery(id+"F0.wireOp",EDGE,"E5");var subQ4=sQuery(id+"F0.wireOp",EDGE,"E4");var subQ5=sQuery(id+"F0.wireOp",EDGE,"E22.filletArc");var subQ6=sQuery(id+"F0.wireOp",EDGE,"E1.bottom");var subQ7=sQuery(id+"F0.wireOp",EDGE,"E1.right");var subQ8=sQuery(id+"F0.wireOp",EDGE,"E1.top");var subQ9=sQuery(id+"F0.wireOp",EDGE,"E1.left");var subQ10=sQuery(id+"F0.wireOp",EDGE,"E23.filletArc");var subQ11=sQuery(id+"F0.wireOp",EDGE,"E24.filletArc");Q0=makeQuery(id+"F2.boolean.opBoolean","SPLIT",FACE,{"disambiguationData":[TD([makeQuery(id+"F1.opExtrude","SWEPT_FACE",FACE,{"disambiguationData":[OSD([subQ6])]})])],"derivedFrom":makeQuery(id+"F1.opExtrude","CAP_FACE",FACE,{"disambiguationData":[OSD([subQ6,subQ8,subQ9,subQ7,subQ4,subQ3,subQ2,subQ1,subQ0,subQ5,subQ10,subQ11])],"isStart":true})});}
            var sketch = newSketch(context, id + "F16", { "sketchPlane" : qUnion([Q0])});
            skLineSegment(sketch, "E79", {"start": v(0, 80) * mm, "end": v(0, 110) * mm, "construction": true});
            skCircle(sketch, "E80", {"center": v(0, 110) * mm, "radius": 6 * mm});
            skLineSegment(sketch, "E81", {"start": v(-33, 80) * mm, "end": v(-15, 98) * mm});
            skLineSegment(sketch, "E82", {"start": v(15, 98) * mm, "end": v(33, 80) * mm});
            skLineSegment(sketch, "E83", {"start": v(15, 110) * mm, "end": v(15, 98) * mm});
            skLineSegment(sketch, "E84", {"start": v(-15, 110) * mm, "end": v(-15, 98) * mm});
            skArc(sketch, "E85", {"start": v(15, 110) * mm, "mid": v(0, 125) * mm, "end": v(-15, 110) * mm});
            skLineSegment(sketch, "E86", {"start": v(-90, 0) * mm, "end": v(90, 0) * mm, "construction": true});
            skArc(sketch, "E87.MirrorCS", {"start": v(15, -110) * mm, "mid": v(0, -125) * mm, "end": v(-15, -110) * mm});
            skLineSegment(sketch, "E88.MirrorCS", {"start": v(15, -110) * mm, "end": v(15, -98) * mm});
            skLineSegment(sketch, "E89.MirrorCS", {"start": v(15, -98) * mm, "end": v(33, -80) * mm});
            skLineSegment(sketch, "E90.MirrorCS", {"start": v(-33, -80) * mm, "end": v(-15, -98) * mm});
            skLineSegment(sketch, "E91.MirrorCS", {"start": v(-15, -110) * mm, "end": v(-15, -98) * mm});
            skCircle(sketch, "E92.MirrorC", {"center": v(0, -110) * mm, "radius": 6 * mm});
            skLineSegment(sketch, "E93.MirrorCS", {"start": v(0, -80) * mm, "end": v(0, -110) * mm, "construction": true});
            skText(sketch, "E94", { "text": "jill dougherty \n", "fontName": "OpenSans-Regular.ttf"});
            skText(sketch, "E95", { "text": "volume = 57546.334 mm3", "fontName": "OpenSans-Regular.ttf"});
            const initialGuessF16  = {"E94": [-0.12398, -0.14444, 1, 0, 0.0116], "E95": [-0.12398, -0.186, 1, 0, 0.01489]};
            skSetInitialGuess(sketch, initialGuessF16);
            skSolve(sketch);
        }
        {
            var Q0;
            Q0=makeQuery(id+"F16.imprint","IMPRINT",FACE,{"disambiguationData":[TD([[makeQuery(id+"F16.imprint","IMPRINT",EDGE,{"derivedFrom":sQuery(id+"F16.wireOp",EDGE,"E94.sketch_text.stroke-0")}),-1.0]])]});
            var Q1;
            Q1=makeQuery(id+"F16.imprint","IMPRINT",FACE,{"disambiguationData":[TD([[makeQuery(id+"F16.imprint","IMPRINT",EDGE,{"derivedFrom":sQuery(id+"F16.wireOp",EDGE,"E94.sketch_text.stroke-9")}),-1.0]])]});
            var Q2;
            Q2=makeQuery(id+"F16.imprint","IMPRINT",FACE,{"disambiguationData":[TD([[makeQuery(id+"F16.imprint","IMPRINT",EDGE,{"derivedFrom":sQuery(id+"F16.wireOp",EDGE,"E94.sketch_text.stroke-17")}),-1.0]])]});
            var Q3;
            Q3=makeQuery(id+"F16.imprint","IMPRINT",FACE,{"disambiguationData":[TD([[makeQuery(id+"F16.imprint","IMPRINT",EDGE,{"derivedFrom":sQuery(id+"F16.wireOp",EDGE,"E94.sketch_text.stroke-21")}),-1.0]])]});
            var Q4;
            Q4=makeQuery(id+"F16.imprint","IMPRINT",FACE,{"disambiguationData":[TD([[makeQuery(id+"F16.imprint","IMPRINT",EDGE,{"derivedFrom":sQuery(id+"F16.wireOp",EDGE,"E94.sketch_text.stroke-29")}),-1.0]])]});
            var Q5;
            Q5=makeQuery(id+"F16.imprint","IMPRINT",FACE,{"disambiguationData":[TD([[makeQuery(id+"F16.imprint","IMPRINT",EDGE,{"derivedFrom":sQuery(id+"F16.wireOp",EDGE,"E94.sketch_text.stroke-33")}),-1.0]])]});
            var Q6;
            Q6=makeQuery(id+"F16.imprint","IMPRINT",FACE,{"disambiguationData":[TD([[makeQuery(id+"F16.imprint","IMPRINT",EDGE,{"derivedFrom":sQuery(id+"F16.wireOp",EDGE,"E94.sketch_text.stroke-78")}),-1.0]])]});
            var Q7;
            Q7=makeQuery(id+"F16.imprint","IMPRINT",FACE,{"disambiguationData":[TD([[makeQuery(id+"F16.imprint","IMPRINT",EDGE,{"derivedFrom":sQuery(id+"F16.wireOp",EDGE,"E94.sketch_text.stroke-139")}),-1.0]])]});
            var Q8;
            Q8=makeQuery(id+"F16.imprint","IMPRINT",FACE,{"disambiguationData":[TD([[makeQuery(id+"F16.imprint","IMPRINT",EDGE,{"derivedFrom":sQuery(id+"F16.wireOp",EDGE,"E94.sketch_text.stroke-176")}),-1.0]])]});
            var Q9;
            Q9=makeQuery(id+"F16.imprint","IMPRINT",FACE,{"disambiguationData":[TD([[makeQuery(id+"F16.imprint","IMPRINT",EDGE,{"derivedFrom":sQuery(id+"F16.wireOp",EDGE,"E94.sketch_text.stroke-189")}),-1.0]])]});
            var Q10;
            Q10=makeQuery(id+"F16.imprint","IMPRINT",FACE,{"disambiguationData":[TD([[makeQuery(id+"F16.imprint","IMPRINT",EDGE,{"derivedFrom":sQuery(id+"F16.wireOp",EDGE,"E94.sketch_text.stroke-208")}),-1.0]])]});
            var Q11;
            Q11=makeQuery(id+"F16.imprint","IMPRINT",FACE,{"disambiguationData":[TD([[makeQuery(id+"F16.imprint","IMPRINT",EDGE,{"derivedFrom":sQuery(id+"F16.wireOp",EDGE,"E95.sketch_text.stroke-0")}),-1.0]])]});
            var Q12;
            Q12=makeQuery(id+"F16.imprint","IMPRINT",FACE,{"disambiguationData":[TD([[makeQuery(id+"F16.imprint","IMPRINT",EDGE,{"derivedFrom":sQuery(id+"F16.wireOp",EDGE,"E95.sketch_text.stroke-27")}),-1.0]])]});
            var Q13;
            Q13=makeQuery(id+"F16.imprint","IMPRINT",FACE,{"disambiguationData":[TD([[makeQuery(id+"F16.imprint","IMPRINT",EDGE,{"derivedFrom":sQuery(id+"F16.wireOp",EDGE,"E95.sketch_text.stroke-31")}),-1.0]])]});
            var Q14;
            Q14=makeQuery(id+"F16.imprint","IMPRINT",FACE,{"disambiguationData":[TD([[makeQuery(id+"F16.imprint","IMPRINT",EDGE,{"derivedFrom":sQuery(id+"F16.wireOp",EDGE,"E95.sketch_text.stroke-48")}),-1.0]])]});
            var Q15;
            Q15=makeQuery(id+"F16.imprint","IMPRINT",FACE,{"disambiguationData":[TD([[makeQuery(id+"F16.imprint","IMPRINT",EDGE,{"derivedFrom":sQuery(id+"F16.wireOp",EDGE,"E95.sketch_text.stroke-95")}),-1.0]])]});
            var Q16;
            Q16=makeQuery(id+"F16.imprint","IMPRINT",FACE,{"disambiguationData":[TD([[makeQuery(id+"F16.imprint","IMPRINT",EDGE,{"derivedFrom":sQuery(id+"F16.wireOp",EDGE,"E95.sketch_text.stroke-99")}),-1.0]])]});
            var Q17;
            Q17=makeQuery(id+"F16.imprint","IMPRINT",FACE,{"disambiguationData":[TD([[makeQuery(id+"F16.imprint","IMPRINT",EDGE,{"derivedFrom":sQuery(id+"F16.wireOp",EDGE,"E95.sketch_text.stroke-103")}),-1.0]])]});
            var Q18;
            Q18=makeQuery(id+"F16.imprint","IMPRINT",FACE,{"disambiguationData":[TD([[makeQuery(id+"F16.imprint","IMPRINT",EDGE,{"derivedFrom":sQuery(id+"F16.wireOp",EDGE,"E95.sketch_text.stroke-122")}),-1.0]])]});
            var Q19;
            Q19=makeQuery(id+"F16.imprint","IMPRINT",FACE,{"disambiguationData":[TD([[makeQuery(id+"F16.imprint","IMPRINT",EDGE,{"derivedFrom":sQuery(id+"F16.wireOp",EDGE,"E95.sketch_text.stroke-129")}),-1.0]])]});
            var Q20;
            Q20=makeQuery(id+"F16.imprint","IMPRINT",FACE,{"disambiguationData":[TD([[makeQuery(id+"F16.imprint","IMPRINT",EDGE,{"derivedFrom":sQuery(id+"F16.wireOp",EDGE,"E95.sketch_text.stroke-190")}),-1.0]])]});
            var Q21;
            Q21=makeQuery(id+"F16.imprint","IMPRINT",FACE,{"disambiguationData":[TD([[makeQuery(id+"F16.imprint","IMPRINT",EDGE,{"derivedFrom":sQuery(id+"F16.wireOp",EDGE,"E95.sketch_text.stroke-198")}),-1.0]])]});
            var Q22;
            Q22=makeQuery(id+"F16.imprint","IMPRINT",FACE,{"disambiguationData":[TD([[makeQuery(id+"F16.imprint","IMPRINT",EDGE,{"derivedFrom":sQuery(id+"F16.wireOp",EDGE,"E95.sketch_text.stroke-226")}),-1.0]])]});
            var Q23;
            Q23=makeQuery(id+"F16.imprint","IMPRINT",FACE,{"disambiguationData":[TD([[makeQuery(id+"F16.imprint","IMPRINT",EDGE,{"derivedFrom":sQuery(id+"F16.wireOp",EDGE,"E95.sketch_text.stroke-271")}),-1.0]])]});
            var Q24;
            Q24=makeQuery(id+"F16.imprint","IMPRINT",FACE,{"disambiguationData":[TD([[makeQuery(id+"F16.imprint","IMPRINT",EDGE,{"derivedFrom":sQuery(id+"F16.wireOp",EDGE,"E95.sketch_text.stroke-299")}),-1.0]])]});
            var Q25;
            Q25=makeQuery(id+"F16.imprint","IMPRINT",FACE,{"disambiguationData":[TD([[makeQuery(id+"F16.imprint","IMPRINT",EDGE,{"derivedFrom":sQuery(id+"F16.wireOp",EDGE,"E95.sketch_text.stroke-327")}),-1.0]])]});
            var Q26;
            Q26=makeQuery(id+"F16.imprint","IMPRINT",FACE,{"disambiguationData":[TD([[makeQuery(id+"F16.imprint","IMPRINT",EDGE,{"derivedFrom":sQuery(id+"F16.wireOp",EDGE,"E94.sketch_text.stroke-37")}),-1.0]])]});
            var Q27;
            Q27=makeQuery(id+"F16.imprint","IMPRINT",FACE,{"disambiguationData":[TD([[makeQuery(id+"F16.imprint","IMPRINT",EDGE,{"derivedFrom":sQuery(id+"F16.wireOp",EDGE,"E94.sketch_text.stroke-61")}),-1.0]])]});
            var Q28;
            Q28=makeQuery(id+"F16.imprint","IMPRINT",FACE,{"disambiguationData":[TD([[makeQuery(id+"F16.imprint","IMPRINT",EDGE,{"derivedFrom":sQuery(id+"F16.wireOp",EDGE,"E94.sketch_text.stroke-157")}),-1.0]])]});
            var Q29;
            Q29=makeQuery(id+"F16.imprint","IMPRINT",FACE,{"disambiguationData":[TD([[makeQuery(id+"F16.imprint","IMPRINT",EDGE,{"derivedFrom":sQuery(id+"F16.wireOp",EDGE,"E95.sketch_text.stroke-10")}),-1.0]])]});
            var Q30;
            Q30=makeQuery(id+"F16.imprint","IMPRINT",FACE,{"disambiguationData":[TD([[makeQuery(id+"F16.imprint","IMPRINT",EDGE,{"derivedFrom":sQuery(id+"F16.wireOp",EDGE,"E95.sketch_text.stroke-76")}),-1.0]])]});
            var Q31;
            Q31=makeQuery(id+"F16.imprint","IMPRINT",FACE,{"disambiguationData":[TD([[makeQuery(id+"F16.imprint","IMPRINT",EDGE,{"derivedFrom":sQuery(id+"F16.wireOp",EDGE,"E95.sketch_text.stroke-148")}),-1.0]])]});
            var Q32;
            Q32=makeQuery(id+"F16.imprint","IMPRINT",FACE,{"disambiguationData":[TD([[makeQuery(id+"F16.imprint","IMPRINT",EDGE,{"derivedFrom":sQuery(id+"F16.wireOp",EDGE,"E95.sketch_text.stroke-165")}),-1.0]])]});
            var Q33;
            Q33=makeQuery(id+"F16.imprint","IMPRINT",FACE,{"disambiguationData":[TD([[makeQuery(id+"F16.imprint","IMPRINT",EDGE,{"derivedFrom":sQuery(id+"F16.wireOp",EDGE,"E95.sketch_text.stroke-254")}),-1.0]])]});
            var Q34;
            Q34=makeQuery(id+"F16.imprint","IMPRINT",FACE,{"disambiguationData":[TD([[makeQuery(id+"F16.imprint","IMPRINT",EDGE,{"derivedFrom":sQuery(id+"F16.wireOp",EDGE,"E94.sketch_text.stroke-95")}),-1.0]])]});
            var Q35;
            Q35=makeQuery(id+"F16.imprint","IMPRINT",FACE,{"disambiguationData":[TD([[makeQuery(id+"F16.imprint","IMPRINT",EDGE,{"derivedFrom":sQuery(id+"F16.wireOp",EDGE,"E87.MirrorCS")}),-1.0]])]});
            var Q36;
            {var subQ15=sQuery(id+"F0.wireOp",EDGE,"E1.left");Q36=makeQuery(id+"F16.imprint","IMPRINT",FACE,{"disambiguationData":[TD([[makeQuery(id+"F16.imprint","IMPRINT",EDGE,{"derivedFrom":makeQuery(id+"F1.opExtrude","CAP_EDGE",EDGE,{"disambiguationData":[OSD([subQ15])],"isStart":true})}),-1.0]])]});}
            var Q37;
            Q37=makeQuery(id+"F16.imprint","IMPRINT",FACE,{"disambiguationData":[TD([[makeQuery(id+"F16.imprint","IMPRINT",EDGE,{"derivedFrom":sQuery(id+"F16.wireOp",EDGE,"E80")}),-1.0]])]});
            var Q38;
            Q38=makeQuery(id+"F2.opExtrude","CAP_FACE",FACE,{"disambiguationData":[OSD([sQuery(id+"F0.wireOp",EDGE,"E12"),sQuery(id+"F0.wireOp",EDGE,"E13"),sQuery(id+"F0.wireOp",EDGE,"E14"),sQuery(id+"F0.wireOp",EDGE,"E15"),sQuery(id+"F0.wireOp",EDGE,"E17.filletArc"),sQuery(id+"F0.wireOp",EDGE,"E18.filletArc"),sQuery(id+"F0.wireOp",EDGE,"E19.filletArc"),sQuery(id+"F0.wireOp",EDGE,"E20.filletArc"),sQuery(id+"F0.wireOp",EDGE,"E25.0"),sQuery(id+"F0.wireOp",EDGE,"E25.1"),sQuery(id+"F0.wireOp",EDGE,"E25.2"),sQuery(id+"F0.wireOp",EDGE,"E25.3"),sQuery(id+"F0.wireOp",EDGE,"E25.4"),sQuery(id+"F0.wireOp",EDGE,"E25.5"),sQuery(id+"F0.wireOp",EDGE,"E25.6"),sQuery(id+"F0.wireOp",EDGE,"E25.7")])],"isStart":false});
            extrude(context, id + "F17", {"entities" : qUnion([Q0, Q1, Q2, Q3, Q4, Q5, Q6, Q7, Q8, Q9, Q10, Q11, Q12, Q13, Q14, Q15, Q16, Q17, Q18, Q19, Q20, Q21, Q22, Q23, Q24, Q25, Q26, Q27, Q28, Q29, Q30, Q31, Q32, Q33, Q34, Q35, Q36, Q37]), "operationType" : NewBodyOperationType.ADD, "endBound" : BoundingType.UP_TO_SURFACE, "depth" : 25 * mm, "endBoundEntityFace" : qUnion([Q38]), "offsetDistance" : 25 * mm});
        }
    });
